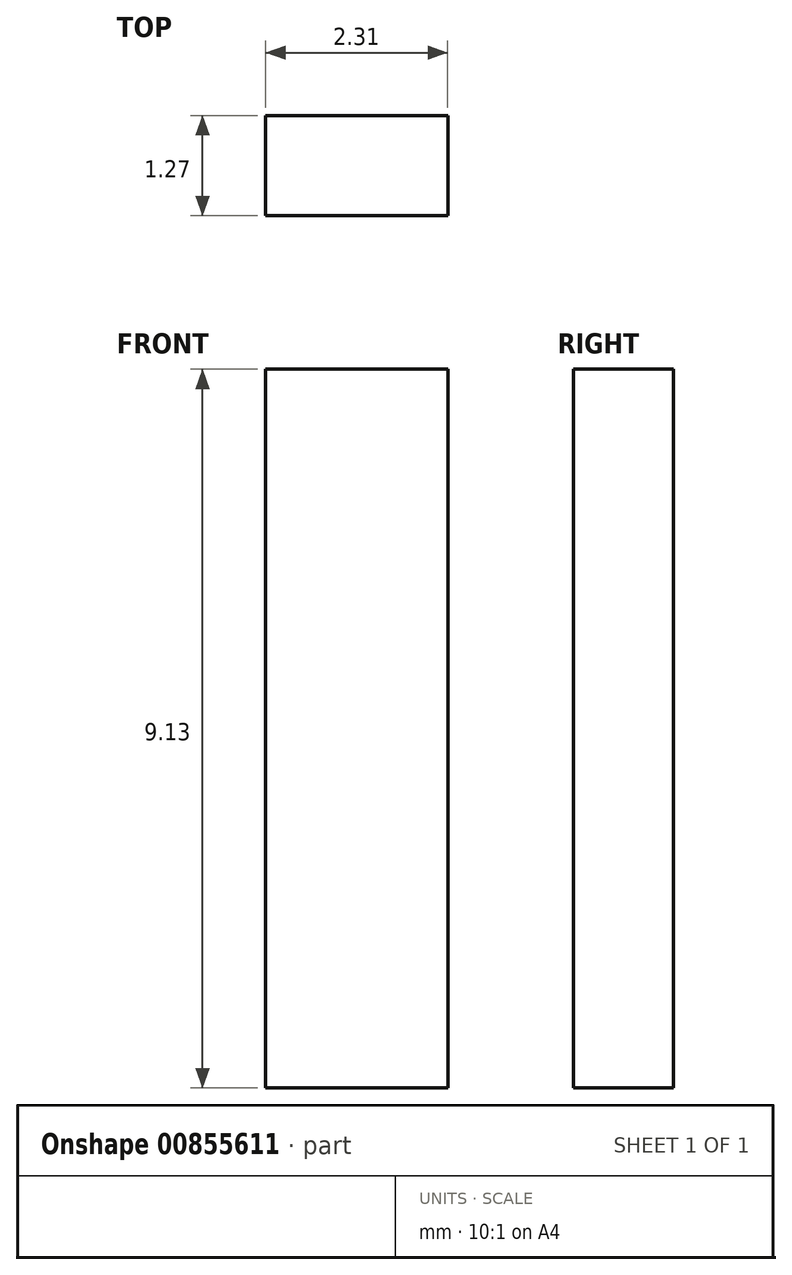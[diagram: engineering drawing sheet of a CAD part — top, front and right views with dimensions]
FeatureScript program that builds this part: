
annotation { "Feature Type Name" : "Feature", "Feature Type Description" : "" }
export const myFeature = defineFeature(function(context is Context, id is Id, definition is map)
    precondition{}
    {
        {
            var Q0;
            Q0=qCreatedBy(makeId("Front.planeOp"),FACE);
            var sketch = newSketch(context, id + "F0", { "sketchPlane" : qUnion([Q0])});
            skCircle(sketch, "E0", {"center": v(0, 0) * mm, "radius": 3.05 * mm});
            skSolve(sketch);
        }
        {
            var Q0;
            Q0=sQuery(id+"F0.wireOp",EDGE,"E0");
            extrude(context, id + "F1", {"bodyType" : ToolBodyType.SURFACE, "surfaceEntities" : qUnion([Q0]), "depth" : 38.1 * mm, "offsetDistance" : 25.4 * mm});
        }
        {
            var Q0;
            Q0=qCreatedBy(makeId("Front.planeOp"),FACE);
            var sketch = newSketch(context, id + "F2", { "sketchPlane" : qUnion([Q0])});
            skLineSegment(sketch, "E1.bottom", {"start": v(1.1, 4.35) * mm, "end": v(-1.22, 4.35) * mm});
            skLineSegment(sketch, "E1.top", {"start": v(1.1, -4.78) * mm, "end": v(-1.22, -4.78) * mm});
            skLineSegment(sketch, "E1.left", {"start": v(1.1, 4.35) * mm, "end": v(1.1, -4.78) * mm});
            skLineSegment(sketch, "E1.right", {"start": v(-1.22, 4.35) * mm, "end": v(-1.22, -4.78) * mm});
            skSolve(sketch);
        }
        {
            var Q0;
            Q0=makeQuery(id+"F2.imprint","IMPRINT",FACE,{"disambiguationData":[TD([[makeQuery(id+"F2.imprint","IMPRINT",EDGE,{"derivedFrom":sQuery(id+"F2.wireOp",EDGE,"E1.bottom")}),1.0]])]});
            extrude(context, id + "F3", {"entities" : qUnion([Q0]), "oppositeDirection" : true, "depth" : 1.27 * mm, "offsetDistance" : 25.4 * mm});
        }
    });
